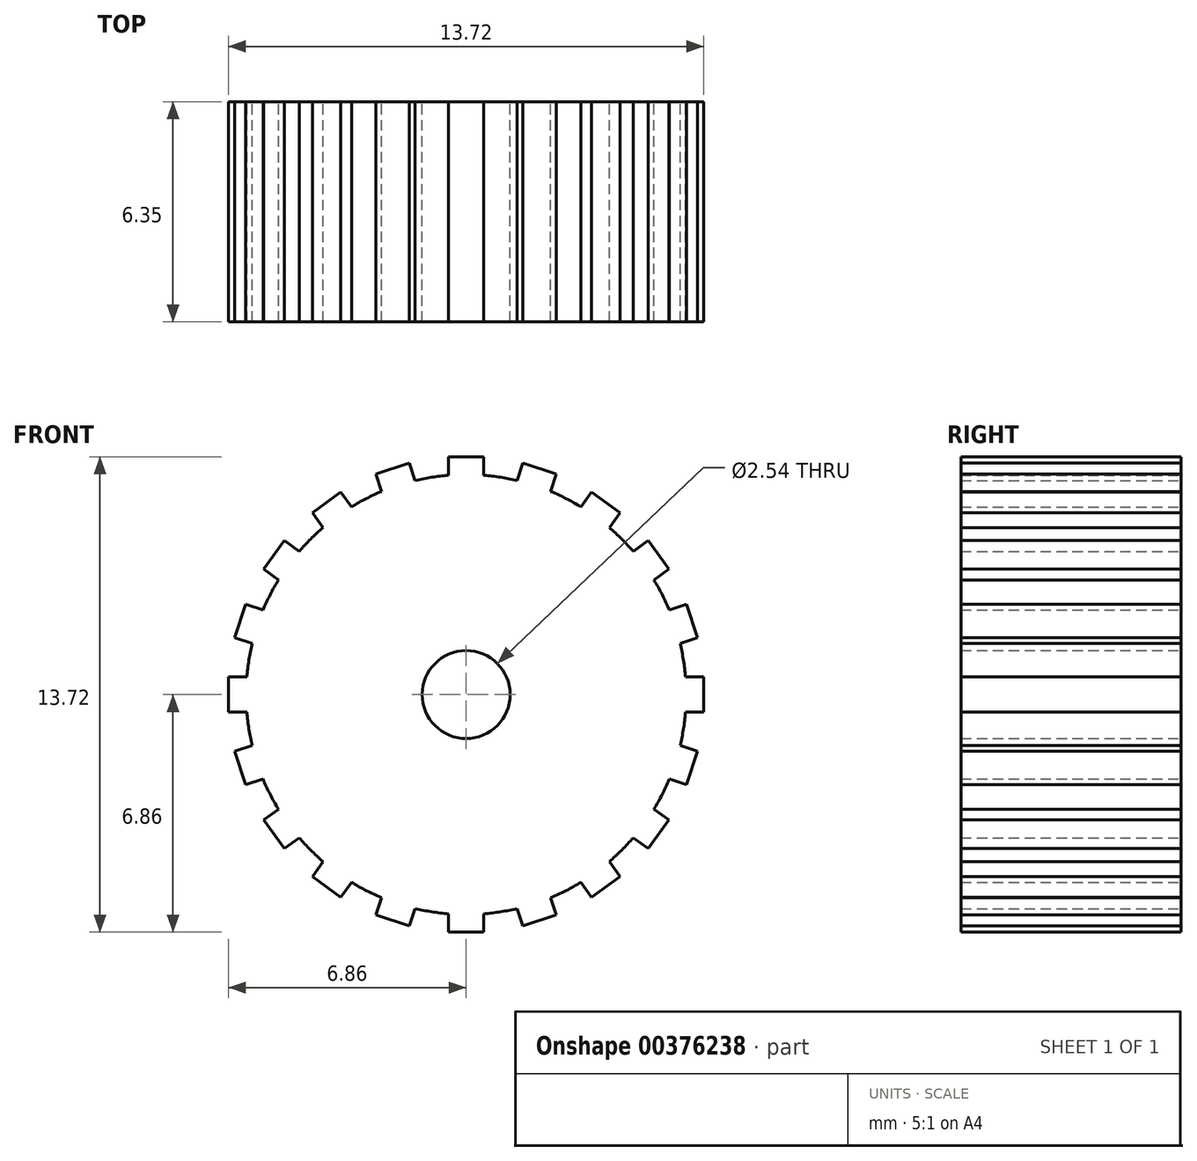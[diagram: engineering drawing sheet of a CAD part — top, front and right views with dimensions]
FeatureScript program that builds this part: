
annotation { "Feature Type Name" : "Feature", "Feature Type Description" : "" }
export const myFeature = defineFeature(function(context is Context, id is Id, definition is map)
    precondition{}
    {
        {
            var Q0;
            Q0=qCreatedBy(makeId("Front.planeOp"),FACE);
            var sketch = newSketch(context, id + "F0", { "sketchPlane" : qUnion([Q0])});
            skCircle(sketch, "E0", {"center": v(0, 0) * mm, "radius": 6.35 * mm});
            skLineSegment(sketch, "E1", {"start": v(0, 6.35) * mm, "end": v(0, 6.86) * mm});
            skLineSegment(sketch, "E2", {"start": v(0, 6.86) * mm, "end": v(0.5, 6.86) * mm});
            skLineSegment(sketch, "E3", {"start": v(0.5, 6.86) * mm, "end": v(0.5, 6.33) * mm});
            skLineSegment(sketch, "E4", {"start": v(0, 6.86) * mm, "end": v(-0.5, 6.86) * mm});
            skLineSegment(sketch, "E5", {"start": v(-0.5, 6.86) * mm, "end": v(-0.5, 6.33) * mm});
            skLineSegment(sketch, "E6.1.0", {"start": v(-1.64, 6.68) * mm, "end": v(-1.47, 6.18) * mm});
            skLineSegment(sketch, "E6.1.1", {"start": v(-2.12, 6.52) * mm, "end": v(-1.64, 6.68) * mm});
            skLineSegment(sketch, "E6.1.2", {"start": v(-2.12, 6.52) * mm, "end": v(-2.6, 6.37) * mm});
            skLineSegment(sketch, "E6.1.3", {"start": v(-2.6, 6.37) * mm, "end": v(-2.44, 5.86) * mm});
            skLineSegment(sketch, "E6.2.0", {"start": v(-3.62, 5.85) * mm, "end": v(-3.3, 5.42) * mm});
            skLineSegment(sketch, "E6.2.1", {"start": v(-4.03, 5.55) * mm, "end": v(-3.62, 5.85) * mm});
            skLineSegment(sketch, "E6.2.2", {"start": v(-4.03, 5.55) * mm, "end": v(-4.44, 5.25) * mm});
            skLineSegment(sketch, "E6.2.3", {"start": v(-4.44, 5.25) * mm, "end": v(-4.13, 4.82) * mm});
            skLineSegment(sketch, "E6.3.0", {"start": v(-5.25, 4.44) * mm, "end": v(-4.82, 4.13) * mm});
            skLineSegment(sketch, "E6.3.1", {"start": v(-5.55, 4.03) * mm, "end": v(-5.25, 4.44) * mm});
            skLineSegment(sketch, "E6.3.2", {"start": v(-5.55, 4.03) * mm, "end": v(-5.85, 3.62) * mm});
            skLineSegment(sketch, "E6.3.3", {"start": v(-5.85, 3.62) * mm, "end": v(-5.42, 3.3) * mm});
            skLineSegment(sketch, "E6.4.0", {"start": v(-6.37, 2.6) * mm, "end": v(-5.86, 2.44) * mm});
            skLineSegment(sketch, "E6.4.1", {"start": v(-6.52, 2.12) * mm, "end": v(-6.37, 2.6) * mm});
            skLineSegment(sketch, "E6.4.2", {"start": v(-6.52, 2.12) * mm, "end": v(-6.68, 1.64) * mm});
            skLineSegment(sketch, "E6.4.3", {"start": v(-6.68, 1.64) * mm, "end": v(-6.18, 1.47) * mm});
            skLineSegment(sketch, "E6.5.0", {"start": v(-6.86, 0.5) * mm, "end": v(-6.33, 0.5) * mm});
            skLineSegment(sketch, "E6.5.1", {"start": v(-6.86, 0) * mm, "end": v(-6.86, 0.5) * mm});
            skLineSegment(sketch, "E6.5.2", {"start": v(-6.86, 0) * mm, "end": v(-6.86, -0.5) * mm});
            skLineSegment(sketch, "E6.5.3", {"start": v(-6.86, -0.5) * mm, "end": v(-6.33, -0.5) * mm});
            skLineSegment(sketch, "E6.6.0", {"start": v(-6.68, -1.64) * mm, "end": v(-6.18, -1.47) * mm});
            skLineSegment(sketch, "E6.6.1", {"start": v(-6.52, -2.12) * mm, "end": v(-6.68, -1.64) * mm});
            skLineSegment(sketch, "E6.6.2", {"start": v(-6.52, -2.12) * mm, "end": v(-6.37, -2.6) * mm});
            skLineSegment(sketch, "E6.6.3", {"start": v(-6.37, -2.6) * mm, "end": v(-5.86, -2.44) * mm});
            skLineSegment(sketch, "E6.7.0", {"start": v(-5.85, -3.62) * mm, "end": v(-5.42, -3.3) * mm});
            skLineSegment(sketch, "E6.7.1", {"start": v(-5.55, -4.03) * mm, "end": v(-5.85, -3.62) * mm});
            skLineSegment(sketch, "E6.7.2", {"start": v(-5.55, -4.03) * mm, "end": v(-5.25, -4.44) * mm});
            skLineSegment(sketch, "E6.7.3", {"start": v(-5.25, -4.44) * mm, "end": v(-4.82, -4.13) * mm});
            skLineSegment(sketch, "E6.8.0", {"start": v(-4.44, -5.25) * mm, "end": v(-4.13, -4.82) * mm});
            skLineSegment(sketch, "E6.8.1", {"start": v(-4.03, -5.55) * mm, "end": v(-4.44, -5.25) * mm});
            skLineSegment(sketch, "E6.8.2", {"start": v(-4.03, -5.55) * mm, "end": v(-3.62, -5.85) * mm});
            skLineSegment(sketch, "E6.8.3", {"start": v(-3.62, -5.85) * mm, "end": v(-3.3, -5.42) * mm});
            skLineSegment(sketch, "E6.9.0", {"start": v(-2.6, -6.37) * mm, "end": v(-2.44, -5.86) * mm});
            skLineSegment(sketch, "E6.9.1", {"start": v(-2.12, -6.52) * mm, "end": v(-2.6, -6.37) * mm});
            skLineSegment(sketch, "E6.9.2", {"start": v(-2.12, -6.52) * mm, "end": v(-1.64, -6.68) * mm});
            skLineSegment(sketch, "E6.9.3", {"start": v(-1.64, -6.68) * mm, "end": v(-1.47, -6.18) * mm});
            skLineSegment(sketch, "E6.10.0", {"start": v(-0.5, -6.86) * mm, "end": v(-0.5, -6.33) * mm});
            skLineSegment(sketch, "E6.10.1", {"start": v(0, -6.86) * mm, "end": v(-0.5, -6.86) * mm});
            skLineSegment(sketch, "E6.10.2", {"start": v(0, -6.86) * mm, "end": v(0.5, -6.86) * mm});
            skLineSegment(sketch, "E6.10.3", {"start": v(0.5, -6.86) * mm, "end": v(0.5, -6.33) * mm});
            skLineSegment(sketch, "E6.11.0", {"start": v(1.64, -6.68) * mm, "end": v(1.47, -6.18) * mm});
            skLineSegment(sketch, "E6.11.1", {"start": v(2.12, -6.52) * mm, "end": v(1.64, -6.68) * mm});
            skLineSegment(sketch, "E6.11.2", {"start": v(2.12, -6.52) * mm, "end": v(2.6, -6.37) * mm});
            skLineSegment(sketch, "E6.11.3", {"start": v(2.6, -6.37) * mm, "end": v(2.44, -5.86) * mm});
            skLineSegment(sketch, "E6.12.0", {"start": v(3.62, -5.85) * mm, "end": v(3.3, -5.42) * mm});
            skLineSegment(sketch, "E6.12.1", {"start": v(4.03, -5.55) * mm, "end": v(3.62, -5.85) * mm});
            skLineSegment(sketch, "E6.12.2", {"start": v(4.03, -5.55) * mm, "end": v(4.44, -5.25) * mm});
            skLineSegment(sketch, "E6.12.3", {"start": v(4.44, -5.25) * mm, "end": v(4.13, -4.82) * mm});
            skLineSegment(sketch, "E6.13.0", {"start": v(5.25, -4.44) * mm, "end": v(4.82, -4.13) * mm});
            skLineSegment(sketch, "E6.13.1", {"start": v(5.55, -4.03) * mm, "end": v(5.25, -4.44) * mm});
            skLineSegment(sketch, "E6.13.2", {"start": v(5.55, -4.03) * mm, "end": v(5.85, -3.62) * mm});
            skLineSegment(sketch, "E6.13.3", {"start": v(5.85, -3.62) * mm, "end": v(5.42, -3.3) * mm});
            skLineSegment(sketch, "E6.14.0", {"start": v(6.37, -2.6) * mm, "end": v(5.86, -2.44) * mm});
            skLineSegment(sketch, "E6.14.1", {"start": v(6.52, -2.12) * mm, "end": v(6.37, -2.6) * mm});
            skLineSegment(sketch, "E6.14.2", {"start": v(6.52, -2.12) * mm, "end": v(6.68, -1.64) * mm});
            skLineSegment(sketch, "E6.14.3", {"start": v(6.68, -1.64) * mm, "end": v(6.18, -1.47) * mm});
            skLineSegment(sketch, "E6.15.0", {"start": v(6.86, -0.5) * mm, "end": v(6.33, -0.5) * mm});
            skLineSegment(sketch, "E6.15.1", {"start": v(6.86, 0) * mm, "end": v(6.86, -0.5) * mm});
            skLineSegment(sketch, "E6.15.2", {"start": v(6.86, 0) * mm, "end": v(6.86, 0.5) * mm});
            skLineSegment(sketch, "E6.15.3", {"start": v(6.86, 0.5) * mm, "end": v(6.33, 0.5) * mm});
            skLineSegment(sketch, "E6.16.0", {"start": v(6.68, 1.64) * mm, "end": v(6.18, 1.47) * mm});
            skLineSegment(sketch, "E6.16.1", {"start": v(6.52, 2.12) * mm, "end": v(6.68, 1.64) * mm});
            skLineSegment(sketch, "E6.16.2", {"start": v(6.52, 2.12) * mm, "end": v(6.37, 2.6) * mm});
            skLineSegment(sketch, "E6.16.3", {"start": v(6.37, 2.6) * mm, "end": v(5.86, 2.44) * mm});
            skLineSegment(sketch, "E6.17.0", {"start": v(5.85, 3.62) * mm, "end": v(5.42, 3.3) * mm});
            skLineSegment(sketch, "E6.17.1", {"start": v(5.55, 4.03) * mm, "end": v(5.85, 3.62) * mm});
            skLineSegment(sketch, "E6.17.2", {"start": v(5.55, 4.03) * mm, "end": v(5.25, 4.44) * mm});
            skLineSegment(sketch, "E6.17.3", {"start": v(5.25, 4.44) * mm, "end": v(4.82, 4.13) * mm});
            skLineSegment(sketch, "E6.18.0", {"start": v(4.44, 5.25) * mm, "end": v(4.13, 4.82) * mm});
            skLineSegment(sketch, "E6.18.1", {"start": v(4.03, 5.55) * mm, "end": v(4.44, 5.25) * mm});
            skLineSegment(sketch, "E6.18.2", {"start": v(4.03, 5.55) * mm, "end": v(3.62, 5.85) * mm});
            skLineSegment(sketch, "E6.18.3", {"start": v(3.62, 5.85) * mm, "end": v(3.3, 5.42) * mm});
            skLineSegment(sketch, "E6.19.0", {"start": v(2.6, 6.37) * mm, "end": v(2.44, 5.86) * mm});
            skLineSegment(sketch, "E6.19.1", {"start": v(2.12, 6.52) * mm, "end": v(2.6, 6.37) * mm});
            skLineSegment(sketch, "E6.19.2", {"start": v(2.12, 6.52) * mm, "end": v(1.64, 6.68) * mm});
            skLineSegment(sketch, "E6.19.3", {"start": v(1.64, 6.68) * mm, "end": v(1.47, 6.18) * mm});
            skCircle(sketch, "E7", {"center": v(0, 0) * mm, "radius": 1.27 * mm});
            skSolve(sketch);
        }
        {
            var Q0;
            Q0=makeQuery(id+"F0.imprint","IMPRINT",FACE,{"disambiguationData":[TD([[makeQuery(id+"F0.imprint","IMPRINT",EDGE,{"derivedFrom":sQuery(id+"F0.wireOp",EDGE,"Q4qDseiW-scej-sILt-jEnA-joMF2CoWFPTH")}),1.0]])]});
            var Q1;
            {var subQ0=sQuery(id+"F0.wireOp",EDGE,"8b62c8fa-b56c-4b69-b245-8ed633f718e5.10.0");Q1=makeQuery(id+"F0.imprint","IMPRINT",FACE,{"disambiguationData":[TD([[makeQuery(id+"F0.imprint","IMPRINT",EDGE,{"derivedFrom":subQ0}),-1.0]])]});}
            var Q2;
            {var subQ0=sQuery(id+"F0.wireOp",EDGE,"8b62c8fa-b56c-4b69-b245-8ed633f718e5.11.0");Q2=makeQuery(id+"F0.imprint","IMPRINT",FACE,{"disambiguationData":[TD([[makeQuery(id+"F0.imprint","IMPRINT",EDGE,{"derivedFrom":subQ0}),-1.0]])]});}
            var Q3;
            {var subQ0=sQuery(id+"F0.wireOp",EDGE,"KAP0ODDg-Thxb-UIxJ-eKvH-gTu8nEJuhLRE");Q3=makeQuery(id+"F0.imprint","IMPRINT",FACE,{"disambiguationData":[TD([[makeQuery(id+"F0.imprint","IMPRINT",EDGE,{"derivedFrom":subQ0}),-1.0]])]});}
            var Q4;
            {var subQ0=sQuery(id+"F0.wireOp",EDGE,"KAP0ODDg-Thxb-UIxJ-eKvH-gTu8nEJuhLRE");Q4=makeQuery(id+"F0.imprint","IMPRINT",FACE,{"disambiguationData":[TD([[makeQuery(id+"F0.imprint","IMPRINT",EDGE,{"derivedFrom":subQ0}),1.0]])]});}
            var Q5;
            {var subQ0=sQuery(id+"F0.wireOp",EDGE,"8b62c8fa-b56c-4b69-b245-8ed633f718e5.1.0");Q5=makeQuery(id+"F0.imprint","IMPRINT",FACE,{"disambiguationData":[TD([[makeQuery(id+"F0.imprint","IMPRINT",EDGE,{"derivedFrom":subQ0}),-1.0]])]});}
            var Q6;
            {var subQ0=sQuery(id+"F0.wireOp",EDGE,"8b62c8fa-b56c-4b69-b245-8ed633f718e5.2.0");Q6=makeQuery(id+"F0.imprint","IMPRINT",FACE,{"disambiguationData":[TD([[makeQuery(id+"F0.imprint","IMPRINT",EDGE,{"derivedFrom":subQ0}),-1.0]])]});}
            var Q7;
            {var subQ0=sQuery(id+"F0.wireOp",EDGE,"8b62c8fa-b56c-4b69-b245-8ed633f718e5.3.0");Q7=makeQuery(id+"F0.imprint","IMPRINT",FACE,{"disambiguationData":[TD([[makeQuery(id+"F0.imprint","IMPRINT",EDGE,{"derivedFrom":subQ0}),-1.0]])]});}
            var Q8;
            {var subQ0=sQuery(id+"F0.wireOp",EDGE,"8b62c8fa-b56c-4b69-b245-8ed633f718e5.4.0");Q8=makeQuery(id+"F0.imprint","IMPRINT",FACE,{"disambiguationData":[TD([[makeQuery(id+"F0.imprint","IMPRINT",EDGE,{"derivedFrom":subQ0}),-1.0]])]});}
            var Q9;
            {var subQ0=sQuery(id+"F0.wireOp",EDGE,"8b62c8fa-b56c-4b69-b245-8ed633f718e5.5.0");Q9=makeQuery(id+"F0.imprint","IMPRINT",FACE,{"disambiguationData":[TD([[makeQuery(id+"F0.imprint","IMPRINT",EDGE,{"derivedFrom":subQ0}),-1.0]])]});}
            var Q10;
            {var subQ0=sQuery(id+"F0.wireOp",EDGE,"8b62c8fa-b56c-4b69-b245-8ed633f718e5.6.0");Q10=makeQuery(id+"F0.imprint","IMPRINT",FACE,{"disambiguationData":[TD([[makeQuery(id+"F0.imprint","IMPRINT",EDGE,{"derivedFrom":subQ0}),-1.0]])]});}
            var Q11;
            {var subQ0=sQuery(id+"F0.wireOp",EDGE,"8b62c8fa-b56c-4b69-b245-8ed633f718e5.7.0");Q11=makeQuery(id+"F0.imprint","IMPRINT",FACE,{"disambiguationData":[TD([[makeQuery(id+"F0.imprint","IMPRINT",EDGE,{"derivedFrom":subQ0}),-1.0]])]});}
            var Q12;
            {var subQ0=sQuery(id+"F0.wireOp",EDGE,"8b62c8fa-b56c-4b69-b245-8ed633f718e5.8.0");Q12=makeQuery(id+"F0.imprint","IMPRINT",FACE,{"disambiguationData":[TD([[makeQuery(id+"F0.imprint","IMPRINT",EDGE,{"derivedFrom":subQ0}),-1.0]])]});}
            var Q13;
            {var subQ0=sQuery(id+"F0.wireOp",EDGE,"8b62c8fa-b56c-4b69-b245-8ed633f718e5.9.0");Q13=makeQuery(id+"F0.imprint","IMPRINT",FACE,{"disambiguationData":[TD([[makeQuery(id+"F0.imprint","IMPRINT",EDGE,{"derivedFrom":subQ0}),-1.0]])]});}
            var Q14;
            {var subQ0=sQuery(id+"F0.wireOp",EDGE,"E6.1.0");Q14=makeQuery(id+"F0.imprint","IMPRINT",FACE,{"disambiguationData":[TD([[makeQuery(id+"F0.imprint","IMPRINT",EDGE,{"derivedFrom":subQ0}),-1.0]])]});}
            var Q15;
            {var subQ0=sQuery(id+"F0.wireOp",EDGE,"E1");Q15=makeQuery(id+"F0.imprint","IMPRINT",FACE,{"disambiguationData":[TD([[makeQuery(id+"F0.imprint","IMPRINT",EDGE,{"derivedFrom":subQ0}),1.0]])]});}
            var Q16;
            {var subQ0=sQuery(id+"F0.wireOp",EDGE,"E1");Q16=makeQuery(id+"F0.imprint","IMPRINT",FACE,{"disambiguationData":[TD([[makeQuery(id+"F0.imprint","IMPRINT",EDGE,{"derivedFrom":subQ0}),-1.0]])]});}
            var Q17;
            {var subQ0=sQuery(id+"F0.wireOp",EDGE,"E6.19.0");Q17=makeQuery(id+"F0.imprint","IMPRINT",FACE,{"disambiguationData":[TD([[makeQuery(id+"F0.imprint","IMPRINT",EDGE,{"derivedFrom":subQ0}),-1.0]])]});}
            var Q18;
            {var subQ0=sQuery(id+"F0.wireOp",EDGE,"E6.18.0");Q18=makeQuery(id+"F0.imprint","IMPRINT",FACE,{"disambiguationData":[TD([[makeQuery(id+"F0.imprint","IMPRINT",EDGE,{"derivedFrom":subQ0}),-1.0]])]});}
            var Q19;
            {var subQ0=sQuery(id+"F0.wireOp",EDGE,"E6.17.0");Q19=makeQuery(id+"F0.imprint","IMPRINT",FACE,{"disambiguationData":[TD([[makeQuery(id+"F0.imprint","IMPRINT",EDGE,{"derivedFrom":subQ0}),-1.0]])]});}
            var Q20;
            {var subQ0=sQuery(id+"F0.wireOp",EDGE,"E6.10.0");Q20=makeQuery(id+"F0.imprint","IMPRINT",FACE,{"disambiguationData":[TD([[makeQuery(id+"F0.imprint","IMPRINT",EDGE,{"derivedFrom":subQ0}),-1.0]])]});}
            var Q21;
            {var subQ0=sQuery(id+"F0.wireOp",EDGE,"E6.11.0");Q21=makeQuery(id+"F0.imprint","IMPRINT",FACE,{"disambiguationData":[TD([[makeQuery(id+"F0.imprint","IMPRINT",EDGE,{"derivedFrom":subQ0}),-1.0]])]});}
            var Q22;
            {var subQ0=sQuery(id+"F0.wireOp",EDGE,"E6.12.0");Q22=makeQuery(id+"F0.imprint","IMPRINT",FACE,{"disambiguationData":[TD([[makeQuery(id+"F0.imprint","IMPRINT",EDGE,{"derivedFrom":subQ0}),-1.0]])]});}
            var Q23;
            {var subQ0=sQuery(id+"F0.wireOp",EDGE,"E6.13.0");Q23=makeQuery(id+"F0.imprint","IMPRINT",FACE,{"disambiguationData":[TD([[makeQuery(id+"F0.imprint","IMPRINT",EDGE,{"derivedFrom":subQ0}),-1.0]])]});}
            var Q24;
            {var subQ0=sQuery(id+"F0.wireOp",EDGE,"E6.14.0");Q24=makeQuery(id+"F0.imprint","IMPRINT",FACE,{"disambiguationData":[TD([[makeQuery(id+"F0.imprint","IMPRINT",EDGE,{"derivedFrom":subQ0}),-1.0]])]});}
            var Q25;
            {var subQ0=sQuery(id+"F0.wireOp",EDGE,"E6.15.0");Q25=makeQuery(id+"F0.imprint","IMPRINT",FACE,{"disambiguationData":[TD([[makeQuery(id+"F0.imprint","IMPRINT",EDGE,{"derivedFrom":subQ0}),-1.0]])]});}
            var Q26;
            {var subQ0=sQuery(id+"F0.wireOp",EDGE,"E6.16.0");Q26=makeQuery(id+"F0.imprint","IMPRINT",FACE,{"disambiguationData":[TD([[makeQuery(id+"F0.imprint","IMPRINT",EDGE,{"derivedFrom":subQ0}),-1.0]])]});}
            var Q27;
            {var subQ0=sQuery(id+"F0.wireOp",EDGE,"E6.2.0");Q27=makeQuery(id+"F0.imprint","IMPRINT",FACE,{"disambiguationData":[TD([[makeQuery(id+"F0.imprint","IMPRINT",EDGE,{"derivedFrom":subQ0}),-1.0]])]});}
            var Q28;
            {var subQ0=sQuery(id+"F0.wireOp",EDGE,"E6.3.0");Q28=makeQuery(id+"F0.imprint","IMPRINT",FACE,{"disambiguationData":[TD([[makeQuery(id+"F0.imprint","IMPRINT",EDGE,{"derivedFrom":subQ0}),-1.0]])]});}
            var Q29;
            {var subQ0=sQuery(id+"F0.wireOp",EDGE,"E6.4.0");Q29=makeQuery(id+"F0.imprint","IMPRINT",FACE,{"disambiguationData":[TD([[makeQuery(id+"F0.imprint","IMPRINT",EDGE,{"derivedFrom":subQ0}),-1.0]])]});}
            var Q30;
            {var subQ0=sQuery(id+"F0.wireOp",EDGE,"E6.5.0");Q30=makeQuery(id+"F0.imprint","IMPRINT",FACE,{"disambiguationData":[TD([[makeQuery(id+"F0.imprint","IMPRINT",EDGE,{"derivedFrom":subQ0}),-1.0]])]});}
            var Q31;
            {var subQ0=sQuery(id+"F0.wireOp",EDGE,"E0");var subQ18=makeQuery(id+"F0.imprint","INTERSECT",VERTEX,{"derivedFrom":[subQ0,sQuery(id+"F0.wireOp",EDGE,"E6.15.3")]});Q31=makeQuery(id+"F0.imprint","IMPRINT",FACE,{"disambiguationData":[TD([[makeQuery(id+"F0.imprint","IMPRINT",EDGE,{"disambiguationData":[TD([[subQ18,-1.0]])],"derivedFrom":subQ0}),1.0]])]});}
            var Q32;
            {var subQ0=sQuery(id+"F0.wireOp",EDGE,"E6.6.0");Q32=makeQuery(id+"F0.imprint","IMPRINT",FACE,{"disambiguationData":[TD([[makeQuery(id+"F0.imprint","IMPRINT",EDGE,{"derivedFrom":subQ0}),-1.0]])]});}
            var Q33;
            {var subQ0=sQuery(id+"F0.wireOp",EDGE,"E6.7.0");Q33=makeQuery(id+"F0.imprint","IMPRINT",FACE,{"disambiguationData":[TD([[makeQuery(id+"F0.imprint","IMPRINT",EDGE,{"derivedFrom":subQ0}),-1.0]])]});}
            var Q34;
            {var subQ0=sQuery(id+"F0.wireOp",EDGE,"E6.8.0");Q34=makeQuery(id+"F0.imprint","IMPRINT",FACE,{"disambiguationData":[TD([[makeQuery(id+"F0.imprint","IMPRINT",EDGE,{"derivedFrom":subQ0}),-1.0]])]});}
            var Q35;
            {var subQ0=sQuery(id+"F0.wireOp",EDGE,"E6.9.0");Q35=makeQuery(id+"F0.imprint","IMPRINT",FACE,{"disambiguationData":[TD([[makeQuery(id+"F0.imprint","IMPRINT",EDGE,{"derivedFrom":subQ0}),-1.0]])]});}
            extrude(context, id + "F1", {"entities" : qUnion([Q0, Q1, Q2, Q3, Q4, Q5, Q6, Q7, Q8, Q9, Q10, Q11, Q12, Q13, Q14, Q15, Q16, Q17, Q18, Q19, Q20, Q21, Q22, Q23, Q24, Q25, Q26, Q27, Q28, Q29, Q30, Q31, Q32, Q33, Q34, Q35]), "depth" : 6.35 * mm});
        }
    });
